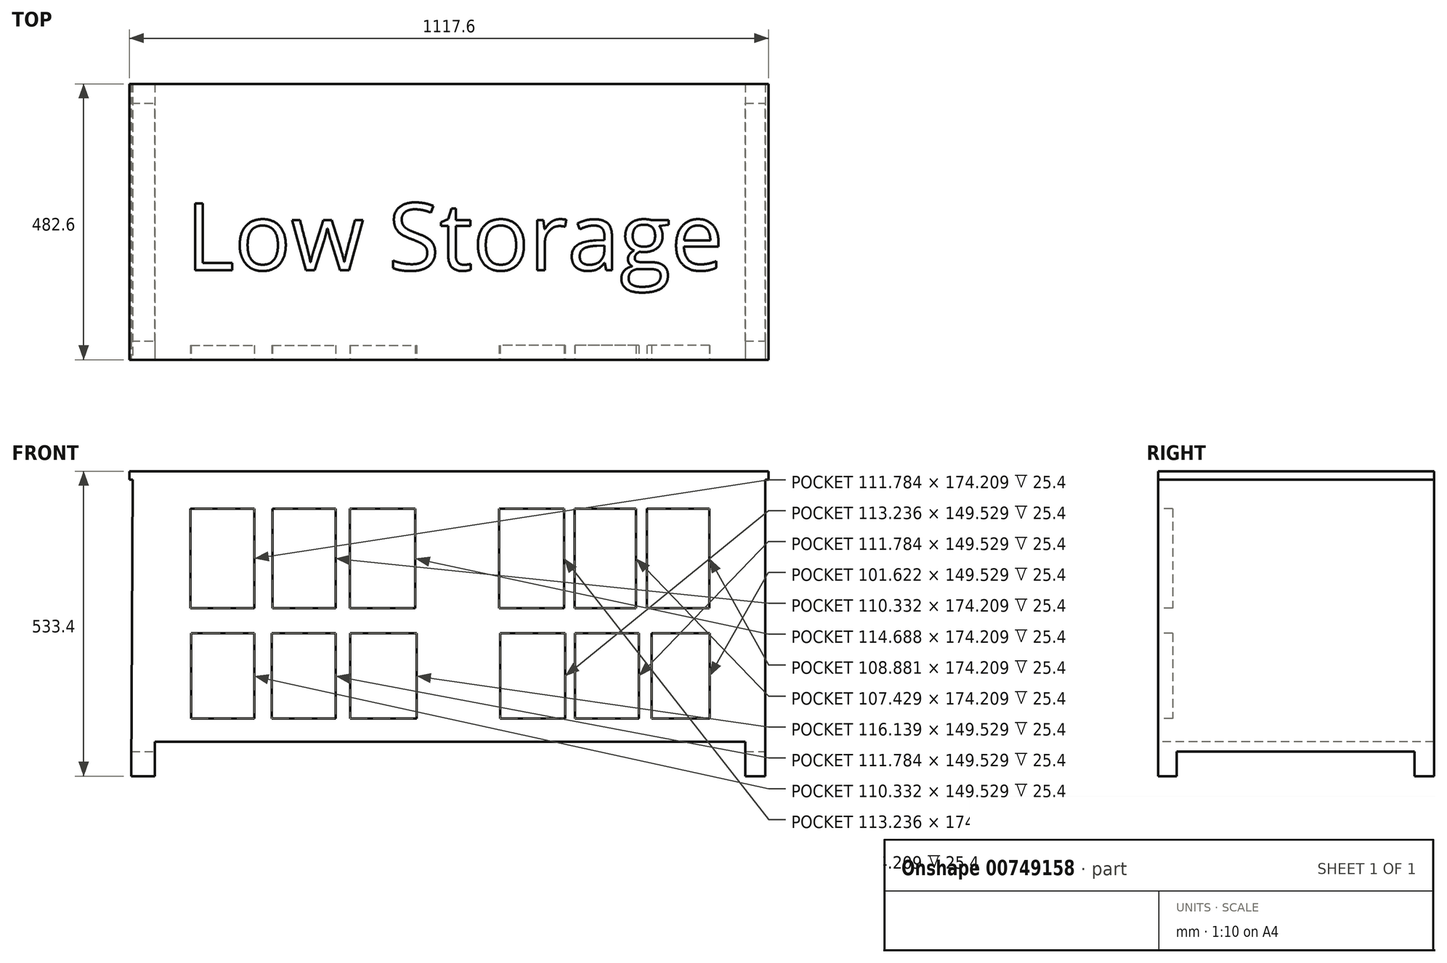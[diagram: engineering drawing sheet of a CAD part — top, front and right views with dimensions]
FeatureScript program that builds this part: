
annotation { "Feature Type Name" : "Feature", "Feature Type Description" : "" }
export const myFeature = defineFeature(function(context is Context, id is Id, definition is map)
    precondition{}
    {
        {
            var Q0;
            Q0=qCreatedBy(makeId("Top.planeOp"),FACE);
            var sketch = newSketch(context, id + "F0", { "sketchPlane" : qUnion([Q0])});
            skLineSegment(sketch, "E0.bottom", {"start": v(0, 0) * mm, "end": v(1117.6, 0) * mm});
            skLineSegment(sketch, "E0.top", {"start": v(0, 482.6) * mm, "end": v(1117.6, 482.6) * mm});
            skLineSegment(sketch, "E0.left", {"start": v(0, 0) * mm, "end": v(0, 482.6) * mm});
            skLineSegment(sketch, "E0.right", {"start": v(1117.6, 0) * mm, "end": v(1117.6, 482.6) * mm});
            skSolve(sketch);
        }
        {
            var Q0;
            Q0 = qSketchRegion(id + "F0", true);
            extrude(context, id + "F1", {"entities" : qUnion([Q0]), "depth" : 533.4 * mm, "offsetDistance" : 25.4 * mm});
        }
        {
            var Q0;
            Q0=makeQuery(id+"F1.opExtrude","SWEPT_FACE",FACE,{"disambiguationData":[OSD([sQuery(id+"F0.wireOp",EDGE,"E0.bottom")])]});
            var sketch = newSketch(context, id + "F2", { "sketchPlane" : qUnion([Q0])});
            skLineSegment(sketch, "E1.bottom", {"start": v(44.66, 0) * mm, "end": v(1076.78, 0) * mm});
            skLineSegment(sketch, "E1.top", {"start": v(44.66, 59.86) * mm, "end": v(1076.78, 59.86) * mm});
            skLineSegment(sketch, "E1.left", {"start": v(44.66, 0) * mm, "end": v(44.66, 59.86) * mm});
            skLineSegment(sketch, "E1.right", {"start": v(1076.78, 0) * mm, "end": v(1076.78, 59.86) * mm});
            skSolve(sketch);
        }
        {
            var Q0;
            Q0 = qSketchRegion(id + "F2", true);
            extrude(context, id + "F3", {"entities" : qUnion([Q0]), "operationType" : NewBodyOperationType.REMOVE, "endBound" : BoundingType.THROUGH_ALL, "oppositeDirection" : true, "depth" : 25.4 * mm, "offsetDistance" : 25.4 * mm});
        }
        {
            var Q0;
            Q0=makeQuery(id+"F1.opExtrude","SWEPT_FACE",FACE,{"disambiguationData":[OSD([sQuery(id+"F0.wireOp",EDGE,"E0.right")])]});
            var sketch = newSketch(context, id + "F4", { "sketchPlane" : qUnion([Q0])});
            skLineSegment(sketch, "E2.bottom", {"start": v(32.84, 0) * mm, "end": v(448.56, 0) * mm});
            skLineSegment(sketch, "E2.top", {"start": v(32.84, 42.71) * mm, "end": v(448.56, 42.71) * mm});
            skLineSegment(sketch, "E2.left", {"start": v(32.84, 0) * mm, "end": v(32.84, 42.71) * mm});
            skLineSegment(sketch, "E2.right", {"start": v(448.56, 0) * mm, "end": v(448.56, 42.71) * mm});
            skSolve(sketch);
        }
        {
            var Q0;
            Q0 = qSketchRegion(id + "F4", true);
            extrude(context, id + "F5", {"entities" : qUnion([Q0]), "operationType" : NewBodyOperationType.REMOVE, "endBound" : BoundingType.THROUGH_ALL, "oppositeDirection" : true, "depth" : 25.4 * mm, "offsetDistance" : 25.4 * mm});
        }
        {
            var Q0;
            Q0=makeQuery(id+"F1.opExtrude","SWEPT_FACE",FACE,{"disambiguationData":[OSD([sQuery(id+"F0.wireOp",EDGE,"E0.bottom")])]});
            var sketch = newSketch(context, id + "F6", { "sketchPlane" : qUnion([Q0])});
            skLineSegment(sketch, "E3.bottom", {"start": v(106.58, 467.77) * mm, "end": v(218.37, 467.77) * mm});
            skLineSegment(sketch, "E3.top", {"start": v(106.58, 293.56) * mm, "end": v(218.37, 293.56) * mm});
            skLineSegment(sketch, "E3.left", {"start": v(106.58, 467.77) * mm, "end": v(106.58, 293.56) * mm});
            skLineSegment(sketch, "E3.right", {"start": v(218.37, 467.77) * mm, "end": v(218.37, 293.56) * mm});
            skLineSegment(sketch, "E4.bottom", {"start": v(250.3, 467.77) * mm, "end": v(360.64, 467.77) * mm});
            skLineSegment(sketch, "E4.top", {"start": v(250.3, 293.56) * mm, "end": v(360.64, 293.56) * mm});
            skLineSegment(sketch, "E4.left", {"start": v(250.3, 467.77) * mm, "end": v(250.3, 293.56) * mm});
            skLineSegment(sketch, "E4.right", {"start": v(360.64, 467.77) * mm, "end": v(360.64, 293.56) * mm});
            skLineSegment(sketch, "E5.bottom", {"start": v(385.32, 467.77) * mm, "end": v(500, 467.77) * mm});
            skLineSegment(sketch, "E5.top", {"start": v(385.32, 293.56) * mm, "end": v(500, 293.56) * mm});
            skLineSegment(sketch, "E5.left", {"start": v(385.32, 467.77) * mm, "end": v(385.32, 293.56) * mm});
            skLineSegment(sketch, "E5.right", {"start": v(500, 467.77) * mm, "end": v(500, 293.56) * mm});
            skLineSegment(sketch, "E6.bottom", {"start": v(1013.92, 467.77) * mm, "end": v(905.04, 467.77) * mm});
            skLineSegment(sketch, "E6.top", {"start": v(1013.92, 293.56) * mm, "end": v(905.04, 293.56) * mm});
            skLineSegment(sketch, "E6.left", {"start": v(1013.92, 467.77) * mm, "end": v(1013.92, 293.56) * mm});
            skLineSegment(sketch, "E6.right", {"start": v(905.04, 467.77) * mm, "end": v(905.04, 293.56) * mm});
            skLineSegment(sketch, "E7.bottom", {"start": v(886.17, 467.77) * mm, "end": v(778.74, 467.77) * mm});
            skLineSegment(sketch, "E7.top", {"start": v(886.17, 293.56) * mm, "end": v(778.74, 293.56) * mm});
            skLineSegment(sketch, "E7.left", {"start": v(886.17, 467.77) * mm, "end": v(886.17, 293.56) * mm});
            skLineSegment(sketch, "E7.right", {"start": v(778.74, 467.77) * mm, "end": v(778.74, 293.56) * mm});
            skLineSegment(sketch, "E8.bottom", {"start": v(759.87, 467.77) * mm, "end": v(646.63, 467.77) * mm});
            skLineSegment(sketch, "E8.top", {"start": v(759.87, 293.56) * mm, "end": v(646.63, 293.56) * mm});
            skLineSegment(sketch, "E8.left", {"start": v(759.87, 467.77) * mm, "end": v(759.87, 293.56) * mm});
            skLineSegment(sketch, "E8.right", {"start": v(646.63, 467.77) * mm, "end": v(646.63, 293.56) * mm});
            skLineSegment(sketch, "E9.bottom", {"start": v(108.03, 250) * mm, "end": v(218.37, 250) * mm});
            skLineSegment(sketch, "E9.top", {"start": v(108.03, 100.48) * mm, "end": v(218.37, 100.48) * mm});
            skLineSegment(sketch, "E9.left", {"start": v(108.03, 250) * mm, "end": v(108.03, 100.48) * mm});
            skLineSegment(sketch, "E9.right", {"start": v(218.37, 250) * mm, "end": v(218.37, 100.48) * mm});
            skLineSegment(sketch, "E10.bottom", {"start": v(248.85, 250) * mm, "end": v(360.64, 250) * mm});
            skLineSegment(sketch, "E10.top", {"start": v(248.85, 100.48) * mm, "end": v(360.64, 100.48) * mm});
            skLineSegment(sketch, "E10.left", {"start": v(248.85, 250) * mm, "end": v(248.85, 100.48) * mm});
            skLineSegment(sketch, "E10.right", {"start": v(360.64, 250) * mm, "end": v(360.64, 100.48) * mm});
            skLineSegment(sketch, "E11.bottom", {"start": v(385.92, 250) * mm, "end": v(502.06, 250) * mm});
            skLineSegment(sketch, "E11.top", {"start": v(385.92, 100.48) * mm, "end": v(502.06, 100.48) * mm});
            skLineSegment(sketch, "E11.left", {"start": v(385.92, 250) * mm, "end": v(385.92, 100.48) * mm});
            skLineSegment(sketch, "E11.right", {"start": v(502.06, 250) * mm, "end": v(502.06, 100.48) * mm});
            skLineSegment(sketch, "E12.bottom", {"start": v(1014.53, 250) * mm, "end": v(912.9, 250) * mm});
            skLineSegment(sketch, "E12.top", {"start": v(1014.53, 100.48) * mm, "end": v(912.9, 100.48) * mm});
            skLineSegment(sketch, "E12.left", {"start": v(1014.53, 250) * mm, "end": v(1014.53, 100.48) * mm});
            skLineSegment(sketch, "E12.right", {"start": v(912.9, 250) * mm, "end": v(912.9, 100.48) * mm});
            skLineSegment(sketch, "E13.bottom", {"start": v(891.13, 250) * mm, "end": v(779.34, 250) * mm});
            skLineSegment(sketch, "E13.top", {"start": v(891.13, 100.48) * mm, "end": v(779.34, 100.48) * mm});
            skLineSegment(sketch, "E13.left", {"start": v(891.13, 250) * mm, "end": v(891.13, 100.48) * mm});
            skLineSegment(sketch, "E13.right", {"start": v(779.34, 250) * mm, "end": v(779.34, 100.48) * mm});
            skLineSegment(sketch, "E14.bottom", {"start": v(761.92, 250) * mm, "end": v(648.69, 250) * mm});
            skLineSegment(sketch, "E14.top", {"start": v(761.92, 100.48) * mm, "end": v(648.69, 100.48) * mm});
            skLineSegment(sketch, "E14.left", {"start": v(761.92, 250) * mm, "end": v(761.92, 100.48) * mm});
            skLineSegment(sketch, "E14.right", {"start": v(648.69, 250) * mm, "end": v(648.69, 100.48) * mm});
            skSolve(sketch);
        }
        {
            var Q0;
            Q0 = qSketchRegion(id + "F6", true);
            extrude(context, id + "F7", {"entities" : qUnion([Q0]), "operationType" : NewBodyOperationType.REMOVE, "oppositeDirection" : true, "depth" : 25.4 * mm, "offsetDistance" : 25.4 * mm});
        }
        {
            var Q0;
            Q0=makeQuery(id+"F1.opExtrude","CAP_FACE",FACE,{"disambiguationData":[OSD([sQuery(id+"F0.wireOp",EDGE,"E0.bottom"),sQuery(id+"F0.wireOp",EDGE,"E0.top"),sQuery(id+"F0.wireOp",EDGE,"E0.left"),sQuery(id+"F0.wireOp",EDGE,"E0.right")])],"isStart":false});
            var sketch = newSketch(context, id + "F8", { "sketchPlane" : qUnion([Q0])});
            skText(sketch, "E15", { "text": "Low Storage", "fontName": "OpenSans-Regular.ttf"});
            const initialGuessF8  = {"E15": [0.09878, 0.15666, 1, 0, 0.1179]};
            skSetInitialGuess(sketch, initialGuessF8);
            skSolve(sketch);
        }
        {
            var Q0;
            Q0 = qSketchRegion(id + "F8", true);
            extrude(context, id + "F9", {"entities" : qUnion([Q0]), "operationType" : NewBodyOperationType.REMOVE, "oppositeDirection" : true, "depth" : 1 / 101.6 * mm, "offsetDistance" : 25.4 * mm});
        }
        {
            var Q0;
            Q0=makeQuery(id+"F1.opExtrude","SWEPT_FACE",FACE,{"disambiguationData":[OSD([sQuery(id+"F0.wireOp",EDGE,"E0.bottom")])]});
            var sketch = newSketch(context, id + "F10", { "sketchPlane" : qUnion([Q0])});
            skLineSegment(sketch, "E16", {"start": v(1117.6, 518.53) * mm, "end": v(1112.2, 518.53) * mm});
            skLineSegment(sketch, "E17", {"start": v(1112.2, 518.53) * mm, "end": v(1112.2, 0) * mm});
            skLineSegment(sketch, "E18", {"start": v(1112.2, 0) * mm, "end": v(1117.6, 0) * mm});
            skLineSegment(sketch, "E19", {"start": v(1117.6, 0) * mm, "end": v(1117.6, 518.53) * mm});
            skLineSegment(sketch, "E20", {"start": v(0, 518.53) * mm, "end": v(5.66, 518.53) * mm});
            skLineSegment(sketch, "E21", {"start": v(5.66, 518.53) * mm, "end": v(3.43, 0) * mm});
            skLineSegment(sketch, "E22", {"start": v(3.43, 0) * mm, "end": v(0, 0) * mm});
            skLineSegment(sketch, "E23", {"start": v(0, 0) * mm, "end": v(0, 518.53) * mm});
            skSolve(sketch);
        }
        {
            var Q0;
            Q0 = qSketchRegion(id + "F10", true);
            extrude(context, id + "F11", {"entities" : qUnion([Q0]), "operationType" : NewBodyOperationType.REMOVE, "endBound" : BoundingType.THROUGH_ALL, "oppositeDirection" : true, "depth" : 25.4 * mm, "offsetDistance" : 25.4 * mm});
        }
    });
